# Revit family: 635-00-001 DN50_80
name_source: partatom
category: Pipe Accessories
units: mm (PartAtom-declared; Revit-internal decimal feet)

## family parameters
Always vertical = No
Cut with Voids When Loaded = No
Part Type = Valve - Breaks Into
Round Connector Dimension = Use Diameter
Shared = No
Work Plane-Based = No

## types (4) — shared parameters
1 = 1 mm  [stored 0.00328084 ft]
10 = 10 mm  [stored 0.0328084 ft]
12 = 11 mm  [stored 0.0360892 ft]
2 = 2 mm  [stored 0.00656168 ft]
4 = 4 mm  [stored 0.0131234 ft]
DN050_PN16_OD_63 = 635-071-00-166
DN065_PN16_OD_75 = 635-091-00-166
DN080_PN16_OD_110 = 635-106-00-166
DN080_PN16_OD_90 = 635-105-00-166
Description_ = AVK SUPA MAXI™ TRANSITION COUPLING, PE100/PN16
Search_table = 635-00-001 DN50_80
URL product pages = https://www.avkvalves.com
zero-valued in all types: Default Elevation

## per-type parameters (varying)
- DN050_PN16_OD_63: Bolt_End_dis=81.5 mm; Bore=25 mm  [stored 0.082021 ft]; Cap_Radius=33.57 mm  [stored 0.110138 ft]; D=100 mm; D1=85 mm; D2=26.4 mm  [stored 0.0866142 ft]; D3=30 mm  [stored 0.0984252 ft]; DN=50 mm; FL_T=69.75 mm; FL_T2=34.88 mm; FLange_T1=89.65 mm; L=540 mm; L1=314 mm; L3=162 mm; L4=178.2 mm; L4-L3=11.34 mm  [stored 0.0372047 ft]; L5=222.75 mm; OD=31.5 mm  [stored 0.103346 ft]; PCD=75 mm; Ring_Dia=45.75 mm; Ring_Dia1=42.09 mm  [stored 0.138091 ft]; Ring_dia2=36.8 mm; Ring_dia3=40.47 mm; Ring_dis=329.7 mm; SR1=24 mm  [stored 0.0787402 ft]; SR2=35.5 mm  [stored 0.11647 ft]; Thickness=6.3 mm  [stored 0.0206693 ft]; ring_dim1=38.72 mm
- DN065_PN16_OD_75: Bolt_End_dis=71.5 mm; Bore=32.5 mm  [stored 0.106627 ft]; Cap_Radius=32.5 mm  [stored 0.106627 ft]; D=113 mm; D1=96.05 mm; D2=37.95 mm  [stored 0.124508 ft]; D3=33.9 mm  [stored 0.11122 ft]; DN=65 mm; FL_T=61.86 mm; FL_T2=30.93 mm; FLange_T1=78.65 mm; L=552 mm; L1=247 mm; L3=165.6 mm; L4=182.16 mm; L4-L3=11.59 mm; L5=227.7 mm; OD=37.5 mm; PCD=86.05 mm; Ring_Dia=60 mm; Ring_Dia1=55.2 mm; Ring_dia2=46.35 mm; Ring_dia3=50.99 mm; Ring_dis=259.35 mm; SR1=34.5 mm  [stored 0.113189 ft]; SR2=45.5 mm  [stored 0.149278 ft]; Thickness=7.5 mm  [stored 0.0246063 ft]; ring_dim1=50.78 mm
- DN080_PN16_OD_90: Bolt_End_dis=59 mm; Bore=40 mm  [stored 0.131234 ft]; Cap_Radius=35 mm  [stored 0.114829 ft]; D=117.5 mm; D1=99.88 mm; D2=45.1 mm  [stored 0.147966 ft]; D3=35.25 mm; DN=80 mm; FL_T=59 mm; FL_T2=29.5 mm; FLange_T1=64.9 mm; L=533 mm; L1=314 mm; L3=159.9 mm; L4=175.89 mm; L4-L3=11.19 mm; L5=219.86 mm; OD=45 mm  [stored 0.147638 ft]; PCD=89.88 mm; Ring_Dia=60 mm; Ring_Dia1=55.2 mm; Ring_dia2=50.1 mm; Ring_dia3=55.11 mm; Ring_dis=329.7 mm; SR1=41 mm  [stored 0.134514 ft]; SR2=53 mm; Thickness=9 mm  [stored 0.0295276 ft]; ring_dim1=50.78 mm
- DN080_PN16_OD_110: Bolt_End_dis=59 mm; Bore=40.05 mm  [stored 0.131398 ft]; Cap_Radius=35 mm  [stored 0.114829 ft]; D=117.5 mm; D1=99.88 mm; D2=45.1 mm  [stored 0.147966 ft]; D3=35.25 mm; DN=80.1 mm; FL_T=59 mm; FL_T2=29.5 mm; FLange_T1=64.9 mm; L=543 mm; L1=281 mm; L3=162.9 mm; L4=179.19 mm; L4-L3=11.4 mm; L5=223.99 mm; OD=55 mm; PCD=89.88 mm; Ring_Dia=60 mm; Ring_Dia1=55.2 mm; Ring_dia2=55.1 mm; Ring_dia3=60.61 mm; Ring_dis=295.05 mm; SR1=41 mm  [stored 0.134514 ft]; SR2=53 mm; Thickness=11 mm  [stored 0.0360892 ft]; ring_dim1=50.78 mm

note: [stored X ft] marks values corroborated as IEEE doubles in the binary element streams (Revit-internal decimal feet)

## geometry (parser evidence)
native form markers: Sweep x3
no freeform markers — native parametric forms only
